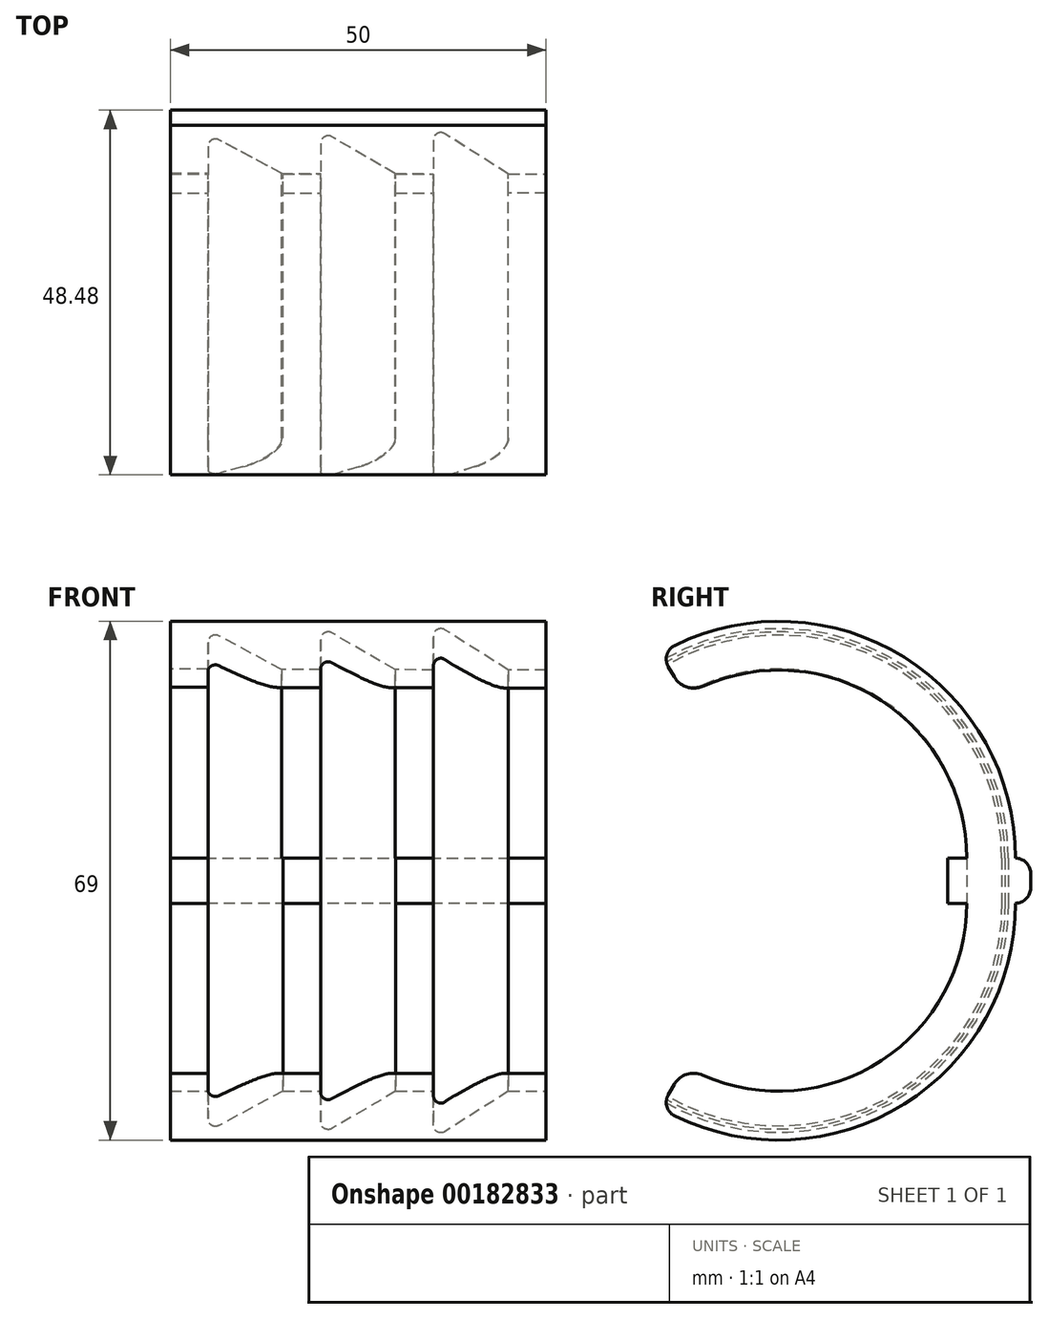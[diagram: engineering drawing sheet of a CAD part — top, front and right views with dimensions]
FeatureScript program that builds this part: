
annotation { "Feature Type Name" : "Feature", "Feature Type Description" : "" }
export const myFeature = defineFeature(function(context is Context, id is Id, definition is map)
    precondition{}
    {
        {
            var Q0;
            Q0=qCreatedBy(makeId("Top.planeOp"),FACE);
            var sketch = newSketch(context, id + "F0", { "sketchPlane" : qUnion([Q0])});
            skLineSegment(sketch, "E0", {"start": v(-24, 11) * mm, "end": v(26, 11) * mm});
            skLineSegment(sketch, "E1", {"start": v(26, 11) * mm, "end": v(26, 0) * mm});
            skLineSegment(sketch, "E2", {"start": v(26, 0) * mm, "end": v(21, 0) * mm});
            skLineSegment(sketch, "E3", {"start": v(21, 0) * mm, "end": v(21, 2.5) * mm});
            skLineSegment(sketch, "E4", {"start": v(6, 0) * mm, "end": v(6, 2.5) * mm});
            skLineSegment(sketch, "E5", {"start": v(-9, 0) * mm, "end": v(-9, 2.5) * mm});
            skLineSegment(sketch, "E6", {"start": v(-24, 11) * mm, "end": v(-24, 0) * mm});
            skLineSegment(sketch, "E7", {"start": v(-24, 0) * mm, "end": v(-19, 0) * mm});
            skLineSegment(sketch, "E8", {"start": v(-9, 0) * mm, "end": v(-4, 0) * mm});
            skLineSegment(sketch, "E9", {"start": v(6, 0) * mm, "end": v(11, 0) * mm});
            skLineSegment(sketch, "E10", {"start": v(21, 2.5) * mm, "end": v(11, 8.85) * mm});
            skLineSegment(sketch, "E11", {"start": v(6, 2.5) * mm, "end": v(-4, 8.35) * mm});
            skLineSegment(sketch, "E12", {"start": v(-9, 2.5) * mm, "end": v(-19, 7.85) * mm});
            skLineSegment(sketch, "E13", {"start": v(-19, 0) * mm, "end": v(-19, 7.85) * mm});
            skLineSegment(sketch, "E14", {"start": v(-4, 0) * mm, "end": v(-4, 8.35) * mm});
            skLineSegment(sketch, "E15", {"start": v(11, 0) * mm, "end": v(11, 8.85) * mm});
            skSolve(sketch);
        }
        {
            var Q0;
            Q0 = qSketchRegion(id + "F0", true);
            extrude(context, id + "F1", {"entities" : qUnion([Q0]), "depth" : 3 * mm});
        }
        {
            var Q0;
            Q0=makeQuery(id+"F1.opExtrude","CAP_FACE",FACE,{"disambiguationData":[OSD([sQuery(id+"F0.wireOp",EDGE,"E0"),sQuery(id+"F0.wireOp",EDGE,"E1"),sQuery(id+"F0.wireOp",EDGE,"E2"),sQuery(id+"F0.wireOp",EDGE,"E3"),sQuery(id+"F0.wireOp",EDGE,"E4"),sQuery(id+"F0.wireOp",EDGE,"E5"),sQuery(id+"F0.wireOp",EDGE,"E6"),sQuery(id+"F0.wireOp",EDGE,"E7"),sQuery(id+"F0.wireOp",EDGE,"E8"),sQuery(id+"F0.wireOp",EDGE,"E9"),sQuery(id+"F0.wireOp",EDGE,"E10"),sQuery(id+"F0.wireOp",EDGE,"E11"),sQuery(id+"F0.wireOp",EDGE,"E12"),sQuery(id+"F0.wireOp",EDGE,"E13"),sQuery(id+"F0.wireOp",EDGE,"E14"),sQuery(id+"F0.wireOp",EDGE,"E15")])],"isStart":true});
            extrude(context, id + "F2", {"entities" : qUnion([Q0]), "operationType" : NewBodyOperationType.ADD, "depth" : 3 * mm});
        }
        {
            var Q0;
            Q0=makeQuery(id+"F2.opExtrude","CAP_FACE",FACE,{"disambiguationData":[OSD([sQuery(id+"F0.wireOp",EDGE,"E0"),sQuery(id+"F0.wireOp",EDGE,"E1"),sQuery(id+"F0.wireOp",EDGE,"E2"),sQuery(id+"F0.wireOp",EDGE,"E3"),sQuery(id+"F0.wireOp",EDGE,"E4"),sQuery(id+"F0.wireOp",EDGE,"E5"),sQuery(id+"F0.wireOp",EDGE,"E6"),sQuery(id+"F0.wireOp",EDGE,"E7"),sQuery(id+"F0.wireOp",EDGE,"E8"),sQuery(id+"F0.wireOp",EDGE,"E9"),sQuery(id+"F0.wireOp",EDGE,"E10"),sQuery(id+"F0.wireOp",EDGE,"E11"),sQuery(id+"F0.wireOp",EDGE,"E12"),sQuery(id+"F0.wireOp",EDGE,"E13"),sQuery(id+"F0.wireOp",EDGE,"E14"),sQuery(id+"F0.wireOp",EDGE,"E15")])],"isStart":false});
            var sketch = newSketch(context, id + "F3", { "sketchPlane" : qUnion([Q0])});
            skLineSegment(sketch, "E16", {"start": v(-24.1, -2.5) * mm, "end": v(26, -2.5) * mm});
            skLineSegment(sketch, "E17", {"start": v(26.05, 22.5) * mm, "end": v(-16.59, 22.5) * mm});
            skLineSegment(sketch, "E18", {"start": v(26, -9) * mm, "end": v(-24, -9) * mm});
            skSolve(sketch);
        }
        {
            var Q0;
            Q0 = qSketchRegion(id + "F3", true);
            var Q1;
            {var subQ0=sQuery(id+"F3.wireOp",EDGE,"E18");Q1=makeQuery(id+"F3.imprint","IMPRINT",FACE,{"disambiguationData":[TD([[makeQuery(id+"F3.imprint","IMPRINT",EDGE,{"derivedFrom":subQ0}),-1.0]])]});}
            var Q2;
            Q2=sQuery(id+"F3.wireOp",EDGE,"E17");
            revolve(context, id + "F4", {"operationType" : NewBodyOperationType.ADD, "entities" : qUnion([Q0, Q1]), "axis" : qUnion([Q2]), "revolveType" : RevolveType.ONE_DIRECTION, "angle" : 120 * degree});
        }
        {
            var Q0;
            {var subQ0=sQuery(id+"F3.wireOp",EDGE,"E16");Q0=makeQuery(id+"F4.opRevolve","CAP_EDGE",EDGE,{"disambiguationData":[OSD([subQ0]),TDD([makeQuery(id+"F3.imprint","IMPRINT",EDGE,{"disambiguationData":[TD([[makeQuery(id+"F3.imprint","INTERSECT",VERTEX,{"derivedFrom":[makeQuery(id+"F2.opExtrude","CAP_EDGE",EDGE,{"disambiguationData":[OSD([sQuery(id+"F0.wireOp",EDGE,"E14")])],"isStart":false}),subQ0]}),1.0]])],"derivedFrom":subQ0})])],"isStart":false});}
            var Q1;
            {var subQ0=sQuery(id+"F3.wireOp",EDGE,"E16");Q1=makeQuery(id+"F4.opRevolve","CAP_EDGE",EDGE,{"disambiguationData":[OSD([subQ0]),TDD([makeQuery(id+"F3.imprint","IMPRINT",EDGE,{"disambiguationData":[TD([[makeQuery(id+"F3.imprint","INTERSECT",VERTEX,{"derivedFrom":[makeQuery(id+"F2.opExtrude","CAP_EDGE",EDGE,{"disambiguationData":[OSD([sQuery(id+"F0.wireOp",EDGE,"E6")])],"isStart":false}),subQ0]}),-1.0]])],"derivedFrom":subQ0})])],"isStart":false});}
            var Q2;
            {var subQ0=sQuery(id+"F3.wireOp",EDGE,"E16");Q2=makeQuery(id+"F4.opRevolve","CAP_EDGE",EDGE,{"disambiguationData":[OSD([subQ0]),TDD([makeQuery(id+"F3.imprint","IMPRINT",EDGE,{"disambiguationData":[TD([[makeQuery(id+"F3.imprint","INTERSECT",VERTEX,{"derivedFrom":[makeQuery(id+"F2.opExtrude","CAP_EDGE",EDGE,{"disambiguationData":[OSD([sQuery(id+"F0.wireOp",EDGE,"E15")])],"isStart":false}),subQ0]}),1.0]])],"derivedFrom":subQ0})])],"isStart":false});}
            var Q3;
            {var subQ0=sQuery(id+"F3.wireOp",EDGE,"E16");Q3=makeQuery(id+"F4.opRevolve","CAP_EDGE",EDGE,{"disambiguationData":[OSD([subQ0]),TDD([makeQuery(id+"F3.imprint","IMPRINT",EDGE,{"disambiguationData":[TD([[makeQuery(id+"F3.imprint","INTERSECT",VERTEX,{"derivedFrom":[makeQuery(id+"F2.opExtrude","CAP_EDGE",EDGE,{"disambiguationData":[OSD([sQuery(id+"F0.wireOp",EDGE,"E1")])],"isStart":false}),subQ0]}),1.0]])],"derivedFrom":subQ0})])],"isStart":false});}
            fillet(context, id + "F5", {"entities" : qUnion([Q0, Q1, Q2, Q3]), "radius" : 3 * mm, "tangentPropagation" : true, "allowEdgeOverflow" : false});
        }
        {
            var Q0;
            {var subQ0=sQuery(id+"F0.wireOp",EDGE,"E15");var subQ1=sQuery(id+"F0.wireOp",EDGE,"E10");Q0=makeQuery(id+"F2.boolean.opBoolean","MERGE",EDGE,{"derivedFrom":[makeQuery(id+"F1.opExtrude","SWEPT_EDGE",EDGE,{"disambiguationData":[OSD([subQ1,subQ0])]}),makeQuery(id+"F2.opExtrude","SWEPT_EDGE",EDGE,{"disambiguationData":[OSD([subQ1,subQ0])]})]});}
            var Q1;
            {var subQ0=sQuery(id+"F0.wireOp",EDGE,"E13");var subQ1=sQuery(id+"F0.wireOp",EDGE,"E12");Q1=makeQuery(id+"F2.boolean.opBoolean","MERGE",EDGE,{"derivedFrom":[makeQuery(id+"F1.opExtrude","SWEPT_EDGE",EDGE,{"disambiguationData":[OSD([subQ1,subQ0])]}),makeQuery(id+"F2.opExtrude","SWEPT_EDGE",EDGE,{"disambiguationData":[OSD([subQ1,subQ0])]})]});}
            var Q2;
            {var subQ0=sQuery(id+"F0.wireOp",EDGE,"E14");var subQ1=sQuery(id+"F0.wireOp",EDGE,"E11");Q2=makeQuery(id+"F2.boolean.opBoolean","MERGE",EDGE,{"derivedFrom":[makeQuery(id+"F1.opExtrude","SWEPT_EDGE",EDGE,{"disambiguationData":[OSD([subQ1,subQ0])]}),makeQuery(id+"F2.opExtrude","SWEPT_EDGE",EDGE,{"disambiguationData":[OSD([subQ1,subQ0])]})]});}
            fillet(context, id + "F6", {"entities" : qUnion([Q0, Q1, Q2]), "radius" : 1 * mm, "tangentPropagation" : true, "allowEdgeOverflow" : false});
        }
        {
            var Q0;
            Q0=makeQuery(id+"F1.opExtrude","CAP_FACE",FACE,{"disambiguationData":[OSD([sQuery(id+"F0.wireOp",EDGE,"E0"),sQuery(id+"F0.wireOp",EDGE,"E1"),sQuery(id+"F0.wireOp",EDGE,"E2"),sQuery(id+"F0.wireOp",EDGE,"E3"),sQuery(id+"F0.wireOp",EDGE,"E4"),sQuery(id+"F0.wireOp",EDGE,"E5"),sQuery(id+"F0.wireOp",EDGE,"E6"),sQuery(id+"F0.wireOp",EDGE,"E7"),sQuery(id+"F0.wireOp",EDGE,"E8"),sQuery(id+"F0.wireOp",EDGE,"E9"),sQuery(id+"F0.wireOp",EDGE,"E10"),sQuery(id+"F0.wireOp",EDGE,"E11"),sQuery(id+"F0.wireOp",EDGE,"E12"),sQuery(id+"F0.wireOp",EDGE,"E13"),sQuery(id+"F0.wireOp",EDGE,"E14"),sQuery(id+"F0.wireOp",EDGE,"E15")])],"isStart":false});
            var sketch = newSketch(context, id + "F7", { "sketchPlane" : qUnion([Q0])});
            skLineSegment(sketch, "E19", {"start": v(-24, 9) * mm, "end": v(26, 9) * mm});
            skLineSegment(sketch, "E20", {"start": v(-24, 2.65) * mm, "end": v(26, 2.5) * mm});
            skLineSegment(sketch, "E21", {"start": v(-24.14, -22.5) * mm, "end": v(26.14, -22.5) * mm});
            skSolve(sketch);
        }
        {
            var Q0;
            Q0 = qSketchRegion(id + "F7", true);
            var Q1;
            {var subQ0=sQuery(id+"F7.wireOp",EDGE,"E19");Q1=makeQuery(id+"F7.imprint","IMPRINT",FACE,{"disambiguationData":[TD([[makeQuery(id+"F7.imprint","IMPRINT",EDGE,{"derivedFrom":subQ0}),-1.0]])]});}
            var Q2;
            Q2=sQuery(id+"F7.wireOp",EDGE,"E21");
            revolve(context, id + "F8", {"operationType" : NewBodyOperationType.ADD, "entities" : qUnion([Q0, Q1]), "axis" : qUnion([Q2]), "revolveType" : RevolveType.ONE_DIRECTION, "angle" : 120 * degree});
        }
        {
            var Q0;
            {var subQ0=sQuery(id+"F7.wireOp",EDGE,"E20");Q0=makeQuery(id+"F8.opRevolve","CAP_EDGE",EDGE,{"disambiguationData":[OSD([subQ0]),TDD([makeQuery(id+"F7.imprint","IMPRINT",EDGE,{"disambiguationData":[TD([[makeQuery(id+"F7.imprint","INTERSECT",VERTEX,{"derivedFrom":[makeQuery(id+"F1.opExtrude","CAP_EDGE",EDGE,{"disambiguationData":[OSD([sQuery(id+"F0.wireOp",EDGE,"E6")])],"isStart":false}),subQ0]}),-1.0]])],"derivedFrom":subQ0})])],"isStart":false});}
            var Q1;
            {var subQ0=sQuery(id+"F7.wireOp",EDGE,"E20");Q1=makeQuery(id+"F8.opRevolve","CAP_EDGE",EDGE,{"disambiguationData":[OSD([subQ0]),TDD([makeQuery(id+"F7.imprint","IMPRINT",EDGE,{"disambiguationData":[TD([[makeQuery(id+"F7.imprint","INTERSECT",VERTEX,{"derivedFrom":[makeQuery(id+"F1.opExtrude","CAP_EDGE",EDGE,{"disambiguationData":[OSD([sQuery(id+"F0.wireOp",EDGE,"E12")])],"isStart":false}),subQ0]}),-1.0]])],"derivedFrom":subQ0})])],"isStart":false});}
            var Q2;
            {var subQ0=sQuery(id+"F7.wireOp",EDGE,"E20");Q2=makeQuery(id+"F8.opRevolve","CAP_EDGE",EDGE,{"disambiguationData":[OSD([subQ0]),TDD([makeQuery(id+"F7.imprint","IMPRINT",EDGE,{"disambiguationData":[TD([[makeQuery(id+"F7.imprint","INTERSECT",VERTEX,{"derivedFrom":[makeQuery(id+"F1.opExtrude","CAP_EDGE",EDGE,{"disambiguationData":[OSD([sQuery(id+"F0.wireOp",EDGE,"E11")])],"isStart":false}),subQ0]}),-1.0]])],"derivedFrom":subQ0})])],"isStart":false});}
            var Q3;
            {var subQ0=sQuery(id+"F7.wireOp",EDGE,"E20");Q3=makeQuery(id+"F8.opRevolve","CAP_EDGE",EDGE,{"disambiguationData":[OSD([subQ0]),TDD([makeQuery(id+"F7.imprint","IMPRINT",EDGE,{"disambiguationData":[TD([[makeQuery(id+"F7.imprint","INTERSECT",VERTEX,{"derivedFrom":[makeQuery(id+"F1.opExtrude","CAP_EDGE",EDGE,{"disambiguationData":[OSD([sQuery(id+"F0.wireOp",EDGE,"E1")])],"isStart":false}),subQ0]}),1.0]])],"derivedFrom":subQ0})])],"isStart":false});}
            fillet(context, id + "F9", {"entities" : qUnion([Q0, Q1, Q2, Q3]), "radius" : 3 * mm, "tangentPropagation" : true, "allowEdgeOverflow" : false});
        }
        {
            var Q0;
            Q0=makeQuery(id+"F2.opExtrude","CAP_EDGE",EDGE,{"disambiguationData":[OSD([sQuery(id+"F0.wireOp",EDGE,"E0")])],"isStart":false});
            var Q1;
            Q1=makeQuery(id+"F1.opExtrude","CAP_EDGE",EDGE,{"disambiguationData":[OSD([sQuery(id+"F0.wireOp",EDGE,"E0")])],"isStart":false});
            fillet(context, id + "F10", {"entities" : qUnion([Q0, Q1]), "radius" : 2 * mm, "tangentPropagation" : true, "allowEdgeOverflow" : false});
        }
        {
            var Q0;
            Q0=makeQuery(id+"F8.opRevolve","CAP_EDGE",EDGE,{"disambiguationData":[OSD([sQuery(id+"F7.wireOp",EDGE,"E19")])],"isStart":false});
            var Q1;
            Q1=makeQuery(id+"F4.opRevolve","CAP_EDGE",EDGE,{"disambiguationData":[OSD([sQuery(id+"F3.wireOp",EDGE,"E18")])],"isStart":false});
            fillet(context, id + "F11", {"entities" : qUnion([Q0, Q1]), "radius" : 2 * mm, "tangentPropagation" : true, "allowEdgeOverflow" : false});
        }
    });
